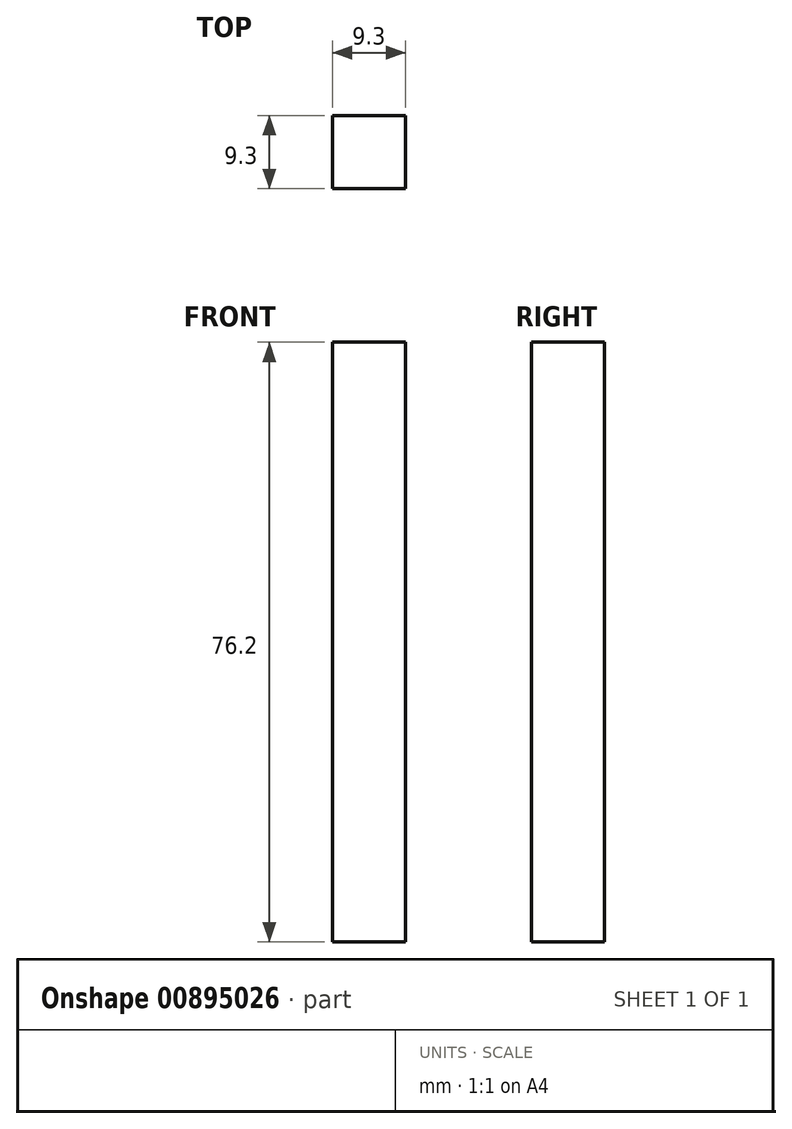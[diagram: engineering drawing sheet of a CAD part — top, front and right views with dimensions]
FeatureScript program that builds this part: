
annotation { "Feature Type Name" : "Feature", "Feature Type Description" : "" }
export const myFeature = defineFeature(function(context is Context, id is Id, definition is map)
    precondition{}
    {
        {
            var Q0;
            Q0=qCreatedBy(makeId("Top.planeOp"),FACE);
            var sketch = newSketch(context, id + "F0", { "sketchPlane" : qUnion([Q0])});
            skLineSegment(sketch, "E0.bottom", {"start": v(4.65, 4.65) * mm, "end": v(-4.65, 4.65) * mm});
            skLineSegment(sketch, "E0.top", {"start": v(4.65, -4.65) * mm, "end": v(-4.65, -4.65) * mm});
            skLineSegment(sketch, "E0.left", {"start": v(4.65, 4.65) * mm, "end": v(4.65, -4.65) * mm});
            skLineSegment(sketch, "E0.right", {"start": v(-4.65, 4.65) * mm, "end": v(-4.65, -4.65) * mm});
            skPoint(sketch, "E0.middle", {"position": v(0, 0) * mm});
            skSolve(sketch);
        }
        {
            var Q0;
            Q0 = qSketchRegion(id + "F0", true);
            extrude(context, id + "F1", {"entities" : qUnion([Q0]), "depth" : 76.2 * mm, "offsetDistance" : 25.4 * mm});
        }
    });
